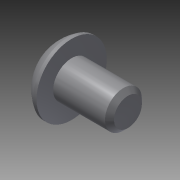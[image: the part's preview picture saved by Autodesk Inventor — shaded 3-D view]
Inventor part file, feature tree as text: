
AUTODESK INVENTOR PART (.ipt)
format: ipt  version: 2015 (Build 190159000, 159)  size: 129,536 bytes
history: native  units: in
note: dims shown in document units (in); Inventor stores cm internally (conversion verified against a paired STEP export)
features: other x3, extrude x1, chamfer x1, imported_body x1, sketch x1
ambient origin geometry x8: Origin, YZ Plane, XZ Plane, XY Plane, X Axis, Y Axis, Z Axis, Center Point
bodies: Body1 (feature_tree)
feature tree (7):
  other  "Bolt 0.25 inch"
  parser-record x1  (decoder bookkeeping rows leaked as tree rows — omitted from the tree; the rows remain in map.json)
  other  "Bolt"
  extrude  "thread length"  Depth=0.25in TaperAngle=0.0deg
  chamfer  "thread chamfer"  Distance=0.02in Angle=45.0deg
  imported_body  "Base1"
  sketch  "Sketch1"  dims[d0=0.164in d1=0.25in d2=0.0in d3=0.02in d4=0.125in d5=45.0deg d7=0.0in d9=0.0in]
